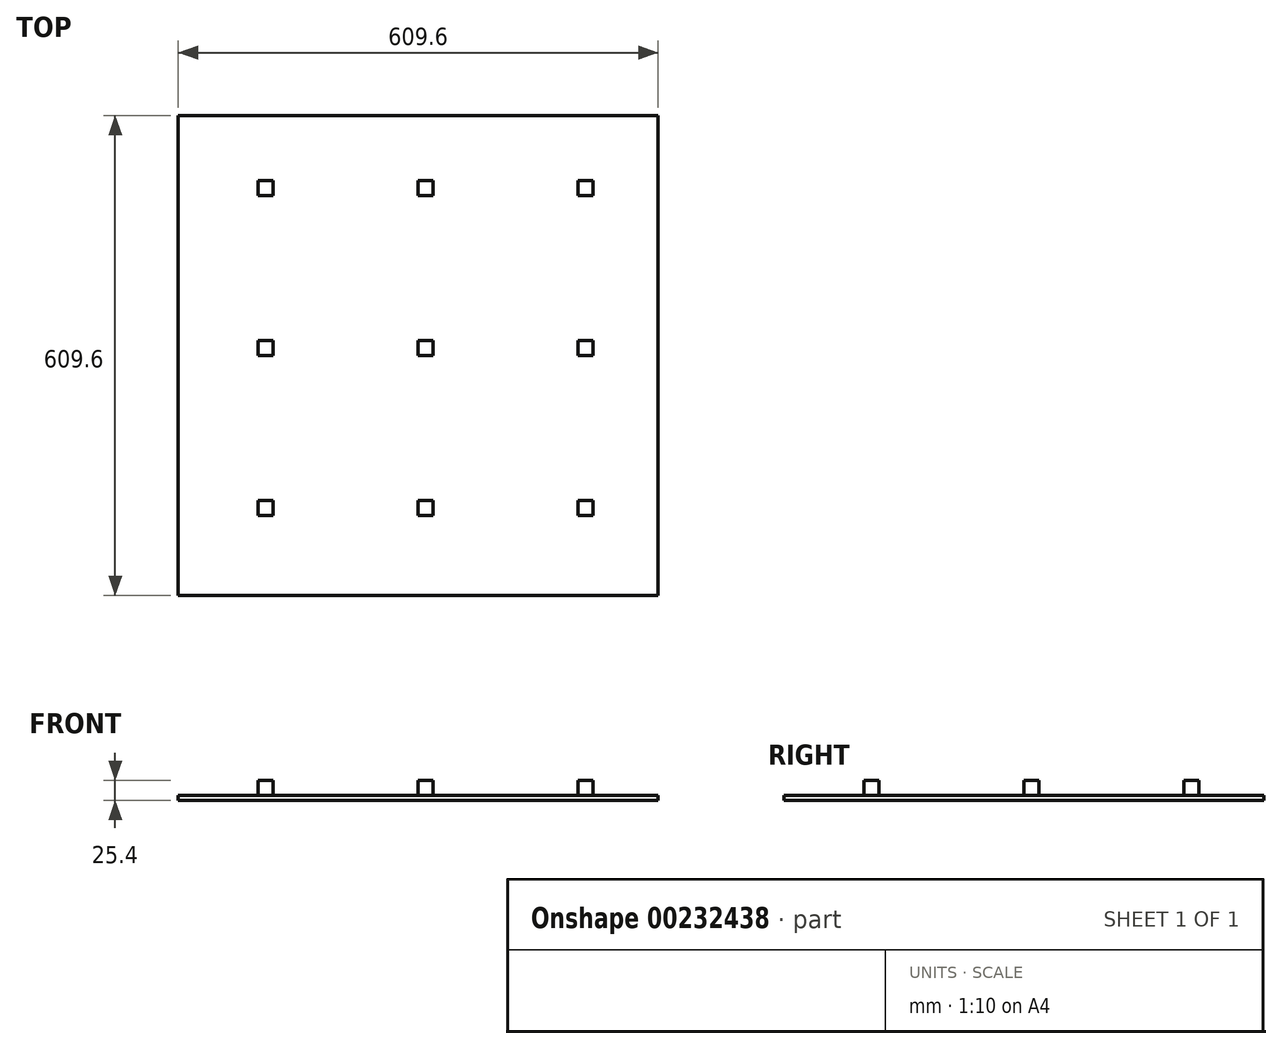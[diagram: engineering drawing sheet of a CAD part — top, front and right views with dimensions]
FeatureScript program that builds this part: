
annotation { "Feature Type Name" : "Feature", "Feature Type Description" : "" }
export const myFeature = defineFeature(function(context is Context, id is Id, definition is map)
    precondition{}
    {
        {
            var Q0;
            Q0=qCreatedBy(makeId("Top.planeOp"),FACE);
            var sketch = newSketch(context, id + "F0", { "sketchPlane" : qUnion([Q0])});
            skLineSegment(sketch, "E0.bottom", {"start": v(0, 0) * mm, "end": v(609.6, 0) * mm});
            skLineSegment(sketch, "E0.top", {"start": v(0, 609.6) * mm, "end": v(609.6, 609.6) * mm});
            skLineSegment(sketch, "E0.left", {"start": v(0, 0) * mm, "end": v(0, 609.6) * mm});
            skLineSegment(sketch, "E0.right", {"start": v(609.6, 0) * mm, "end": v(609.6, 609.6) * mm});
            skSolve(sketch);
        }
        {
            var Q0;
            Q0 = qSketchRegion(id + "F0", true);
            extrude(context, id + "F1", {"entities" : qUnion([Q0]), "depth" : 6.35 * mm});
        }
        {
            var Q0;
            Q0=makeQuery(id+"F1.opExtrude","CAP_FACE",FACE,{"disambiguationData":[OSD([sQuery(id+"F0.wireOp",EDGE,"E0.bottom"),sQuery(id+"F0.wireOp",EDGE,"E0.top"),sQuery(id+"F0.wireOp",EDGE,"E0.left"),sQuery(id+"F0.wireOp",EDGE,"E0.right")])],"isStart":false});
            var sketch = newSketch(context, id + "F2", { "sketchPlane" : qUnion([Q0])});
            skLineSegment(sketch, "E1.bottom", {"start": v(101.6, 120.65) * mm, "end": v(120.65, 120.65) * mm});
            skLineSegment(sketch, "E1.top", {"start": v(101.6, 101.6) * mm, "end": v(120.65, 101.6) * mm});
            skLineSegment(sketch, "E1.left", {"start": v(101.6, 120.65) * mm, "end": v(101.6, 101.6) * mm});
            skLineSegment(sketch, "E1.right", {"start": v(120.65, 120.65) * mm, "end": v(120.65, 101.6) * mm});
            skLineSegment(sketch, "E2.0.1.0", {"start": v(101.6, 323.85) * mm, "end": v(101.6, 304.8) * mm});
            skLineSegment(sketch, "E2.0.1.1", {"start": v(101.6, 323.85) * mm, "end": v(120.65, 323.85) * mm});
            skLineSegment(sketch, "E2.0.1.2", {"start": v(101.6, 304.8) * mm, "end": v(120.65, 304.8) * mm});
            skLineSegment(sketch, "E2.0.1.3", {"start": v(120.65, 323.85) * mm, "end": v(120.65, 304.8) * mm});
            skLineSegment(sketch, "E2.0.2.0", {"start": v(101.6, 527.05) * mm, "end": v(101.6, 508) * mm});
            skLineSegment(sketch, "E2.0.2.1", {"start": v(101.6, 527.05) * mm, "end": v(120.65, 527.05) * mm});
            skLineSegment(sketch, "E2.0.2.2", {"start": v(101.6, 508) * mm, "end": v(120.65, 508) * mm});
            skLineSegment(sketch, "E2.0.2.3", {"start": v(120.65, 527.05) * mm, "end": v(120.65, 508) * mm});
            skLineSegment(sketch, "E2.1.0.0", {"start": v(304.8, 120.65) * mm, "end": v(304.8, 101.6) * mm});
            skLineSegment(sketch, "E2.1.0.1", {"start": v(304.8, 120.65) * mm, "end": v(323.85, 120.65) * mm});
            skLineSegment(sketch, "E2.1.0.2", {"start": v(304.8, 101.6) * mm, "end": v(323.85, 101.6) * mm});
            skLineSegment(sketch, "E2.1.0.3", {"start": v(323.85, 120.65) * mm, "end": v(323.85, 101.6) * mm});
            skLineSegment(sketch, "E2.1.1.0", {"start": v(304.8, 323.85) * mm, "end": v(304.8, 304.8) * mm});
            skLineSegment(sketch, "E2.1.1.1", {"start": v(304.8, 323.85) * mm, "end": v(323.85, 323.85) * mm});
            skLineSegment(sketch, "E2.1.1.2", {"start": v(304.8, 304.8) * mm, "end": v(323.85, 304.8) * mm});
            skLineSegment(sketch, "E2.1.1.3", {"start": v(323.85, 323.85) * mm, "end": v(323.85, 304.8) * mm});
            skLineSegment(sketch, "E2.1.2.0", {"start": v(304.8, 527.05) * mm, "end": v(304.8, 508) * mm});
            skLineSegment(sketch, "E2.1.2.1", {"start": v(304.8, 527.05) * mm, "end": v(323.85, 527.05) * mm});
            skLineSegment(sketch, "E2.1.2.2", {"start": v(304.8, 508) * mm, "end": v(323.85, 508) * mm});
            skLineSegment(sketch, "E2.1.2.3", {"start": v(323.85, 527.05) * mm, "end": v(323.85, 508) * mm});
            skLineSegment(sketch, "E2.2.0.0", {"start": v(508, 120.65) * mm, "end": v(508, 101.6) * mm});
            skLineSegment(sketch, "E2.2.0.1", {"start": v(508, 120.65) * mm, "end": v(527.05, 120.65) * mm});
            skLineSegment(sketch, "E2.2.0.2", {"start": v(508, 101.6) * mm, "end": v(527.05, 101.6) * mm});
            skLineSegment(sketch, "E2.2.0.3", {"start": v(527.05, 120.65) * mm, "end": v(527.05, 101.6) * mm});
            skLineSegment(sketch, "E2.2.1.0", {"start": v(508, 323.85) * mm, "end": v(508, 304.8) * mm});
            skLineSegment(sketch, "E2.2.1.1", {"start": v(508, 323.85) * mm, "end": v(527.05, 323.85) * mm});
            skLineSegment(sketch, "E2.2.1.2", {"start": v(508, 304.8) * mm, "end": v(527.05, 304.8) * mm});
            skLineSegment(sketch, "E2.2.1.3", {"start": v(527.05, 323.85) * mm, "end": v(527.05, 304.8) * mm});
            skLineSegment(sketch, "E2.2.2.0", {"start": v(508, 527.05) * mm, "end": v(508, 508) * mm});
            skLineSegment(sketch, "E2.2.2.1", {"start": v(508, 527.05) * mm, "end": v(527.05, 527.05) * mm});
            skLineSegment(sketch, "E2.2.2.2", {"start": v(508, 508) * mm, "end": v(527.05, 508) * mm});
            skLineSegment(sketch, "E2.2.2.3", {"start": v(527.05, 527.05) * mm, "end": v(527.05, 508) * mm});
            skLineSegment(sketch, "E2.direction1", {"start": v(101.6, 101.6) * mm, "end": v(304.8, 101.6) * mm, "construction": true});
            skLineSegment(sketch, "E2.direction2", {"start": v(101.6, 101.6) * mm, "end": v(101.6, 304.8) * mm, "construction": true});
            skSolve(sketch);
        }
        {
            var Q0;
            Q0 = qSketchRegion(id + "F2", true);
            extrude(context, id + "F3", {"entities" : qUnion([Q0]), "operationType" : NewBodyOperationType.ADD, "depth" : 19.05 * mm});
        }
    });
